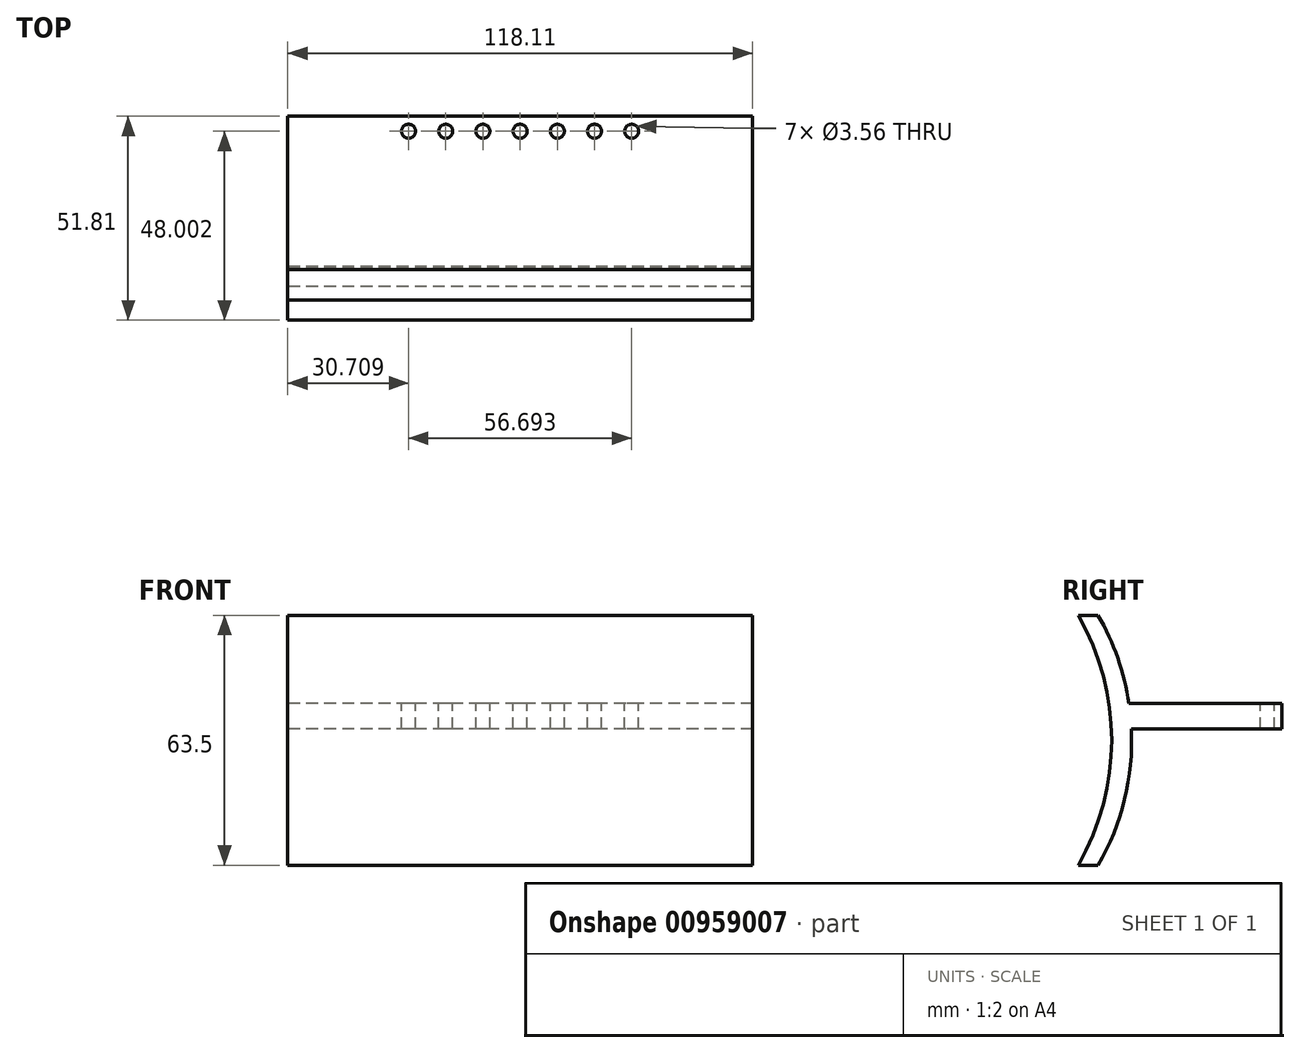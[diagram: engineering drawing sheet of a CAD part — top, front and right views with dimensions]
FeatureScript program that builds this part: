
annotation { "Feature Type Name" : "Feature", "Feature Type Description" : "" }
export const myFeature = defineFeature(function(context is Context, id is Id, definition is map)
    precondition{}
    {
        {
            var Q0;
            Q0=qCreatedBy(makeId("Right.planeOp"),FACE);
            var sketch = newSketch(context, id + "F0", { "sketchPlane" : qUnion([Q0])});
            skArc(sketch, "E0", {"start": v(0, -31.75) * mm, "mid": v(8.5, 0) * mm, "end": v(0, 31.75) * mm});
            skLineSegment(sketch, "E1", {"start": v(0, 31.75) * mm, "end": v(0, -31.75) * mm, "construction": true});
            skLineSegment(sketch, "E2", {"start": v(0, 31.75) * mm, "end": v(5.08, 31.75) * mm});
            skLineSegment(sketch, "E3", {"start": v(5.08, -31.75) * mm, "end": v(0, -31.75) * mm});
            skArc(sketch, "E4", {"start": v(5.08, -31.75) * mm, "mid": v(13.59, 0) * mm, "end": v(5.08, 31.75) * mm});
            skLineSegment(sketch, "E5", {"start": v(0, 2.84) * mm, "end": v(0, -31.75) * mm});
            skSolve(sketch);
        }
        {
            var Q0;
            Q0=makeQuery(id+"F0.imprint","IMPRINT",FACE,{"disambiguationData":[TD([[makeQuery(id+"F0.imprint","IMPRINT",EDGE,{"derivedFrom":sQuery(id+"F0.wireOp",EDGE,"E0")}),-1.0]])]});
            extrude(context, id + "F1", {"entities" : qUnion([Q0]), "depth" : 118.11 * mm, "offsetDistance" : 25.4 * mm});
        }
        {
            var Q0;
            Q0=makeQuery(id+"F1.opExtrude","CAP_FACE",FACE,{"disambiguationData":[OSD([sQuery(id+"F0.wireOp",EDGE,"E0"),sQuery(id+"F0.wireOp",EDGE,"E2"),sQuery(id+"F0.wireOp",EDGE,"E3"),sQuery(id+"F0.wireOp",EDGE,"E4")])],"isStart":true});
            var sketch = newSketch(context, id + "F2", { "sketchPlane" : qUnion([Q0])});
            skLineSegment(sketch, "E6", {"start": v(-13.42, -3.63) * mm, "end": v(-13.48, -3.63) * mm});
            skLineSegment(sketch, "E7", {"start": v(-12.77, 2.84) * mm, "end": v(-12.77, 9.32) * mm});
            skLineSegment(sketch, "E8", {"start": v(-12.77, 2.84) * mm, "end": v(-51.81, 2.84) * mm});
            skLineSegment(sketch, "E9", {"start": v(-51.81, 2.84) * mm, "end": v(-51.81, 9.32) * mm});
            skLineSegment(sketch, "E10", {"start": v(-51.81, 9.32) * mm, "end": v(-12.77, 9.32) * mm});
            skSolve(sketch);
        }
        {
            var Q0;
            Q0 = qSketchRegion(id + "F2", true);
            var Q1;
            Q1=makeQuery(id+"F1.opExtrude","CAP_FACE",FACE,{"disambiguationData":[OSD([sQuery(id+"F0.wireOp",EDGE,"E0"),sQuery(id+"F0.wireOp",EDGE,"E2"),sQuery(id+"F0.wireOp",EDGE,"E3"),sQuery(id+"F0.wireOp",EDGE,"E4")])],"isStart":false});
            extrude(context, id + "F3", {"entities" : qUnion([Q0]), "operationType" : NewBodyOperationType.ADD, "endBound" : BoundingType.UP_TO_SURFACE, "oppositeDirection" : true, "depth" : 25.4 * mm, "endBoundEntityFace" : qUnion([Q1]), "offsetDistance" : 25.4 * mm});
        }
        {
            var Q0;
            Q0=makeQuery(id+"F3.opExtrude","SWEPT_FACE",FACE,{"disambiguationData":[OSD([sQuery(id+"F2.wireOp",EDGE,"E10")])]});
            var sketch = newSketch(context, id + "F4", { "sketchPlane" : qUnion([Q0])});
            skLineSegment(sketch, "E11", {"start": v(0, 48) * mm, "end": v(118.11, 48) * mm, "construction": true});
            skCircle(sketch, "E12", {"center": v(59.06, 48) * mm, "radius": 1.78 * mm});
            skCircle(sketch, "E13", {"center": v(49.6, 48) * mm, "radius": 1.78 * mm});
            skCircle(sketch, "E14", {"center": v(40.16, 48) * mm, "radius": 1.78 * mm});
            skCircle(sketch, "E15", {"center": v(68.5, 48) * mm, "radius": 1.78 * mm});
            skCircle(sketch, "E16", {"center": v(77.95, 48) * mm, "radius": 1.78 * mm});
            skCircle(sketch, "E17", {"center": v(30.7, 48) * mm, "radius": 1.78 * mm});
            skCircle(sketch, "E18", {"center": v(87.4, 48) * mm, "radius": 1.78 * mm});
            skSolve(sketch);
        }
        {
            var Q0;
            Q0 = qSketchRegion(id + "F4", true);
            extrude(context, id + "F5", {"entities" : qUnion([Q0]), "operationType" : NewBodyOperationType.REMOVE, "oppositeDirection" : true, "depth" : 25.4 * mm, "offsetDistance" : 25.4 * mm});
        }
    });
